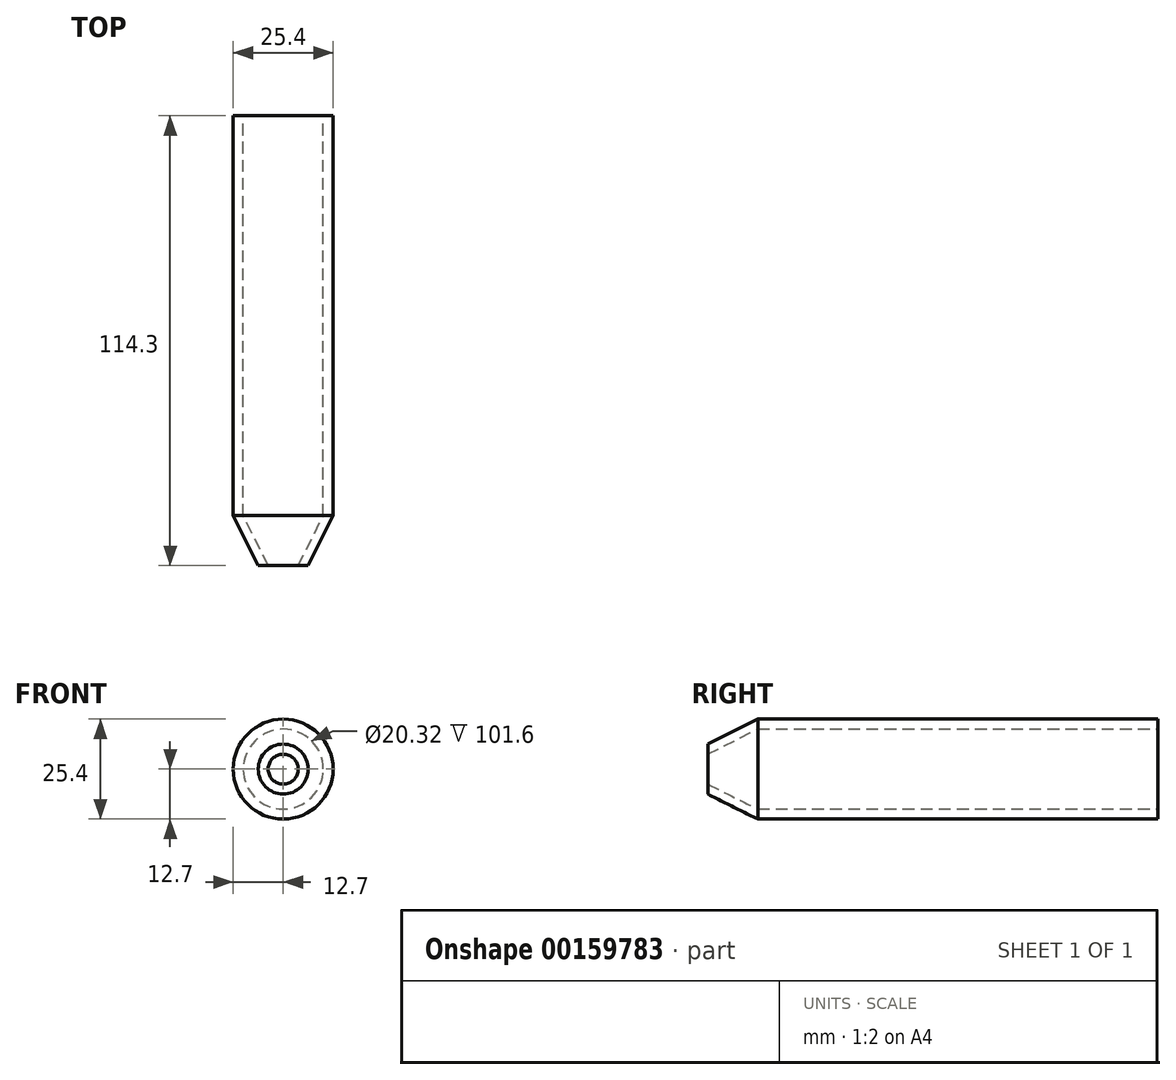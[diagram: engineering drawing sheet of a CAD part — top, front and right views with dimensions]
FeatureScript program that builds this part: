
annotation { "Feature Type Name" : "Feature", "Feature Type Description" : "" }
export const myFeature = defineFeature(function(context is Context, id is Id, definition is map)
    precondition{}
    {
        {
            var Q0;
            Q0=qCreatedBy(makeId("Front.planeOp"),FACE);
            var sketch = newSketch(context, id + "F0", { "sketchPlane" : qUnion([Q0])});
            skCircle(sketch, "E0", {"center": v(0, 0) * mm, "radius": 12.7 * mm});
            skCircle(sketch, "E1", {"center": v(0, 0) * mm, "radius": 10.16 * mm});
            skSolve(sketch);
        }
        {
            var Q0;
            Q0 = qSketchRegion(id + "F0", true);
            extrude(context, id + "F1", {"entities" : qUnion([Q0]), "depth" : 101.6 * mm, "offsetDistance" : 25.4 * mm});
        }
        {
            var Q0;
            Q0=makeQuery(id+"F1.opExtrude","CAP_FACE",FACE,{"disambiguationData":[OSD([sQuery(id+"F0.wireOp",EDGE,"E0"),sQuery(id+"F0.wireOp",EDGE,"E1")])],"isStart":false});
            cPlane(context, id + "F2", {"entities" : qUnion([Q0]), "cplaneType" : CPlaneType.OFFSET, "offset" : 6.35 * mm, "width" : 152.4 * mm, "height" : 152.4 * mm});
        }
        {
            var Q0;
            Q0=qCreatedBy(id+"F2.planeOp",FACE);
            cPlane(context, id + "F3", {"entities" : qUnion([Q0]), "cplaneType" : CPlaneType.OFFSET, "offset" : 6.35 * mm, "width" : 152.4 * mm, "height" : 152.4 * mm});
        }
        {
            var Q0;
            Q0=qCreatedBy(id+"F2.planeOp",FACE);
            var sketch = newSketch(context, id + "F4", { "sketchPlane" : qUnion([Q0])});
            skCircle(sketch, "E2", {"center": v(0, 0) * mm, "radius": 6.99 * mm});
            skCircle(sketch, "E3", {"center": v(0, 0) * mm, "radius": 9.53 * mm});
            skSolve(sketch);
        }
        {
            var Q0;
            Q0=qCreatedBy(id+"F3.planeOp",FACE);
            var sketch = newSketch(context, id + "F5", { "sketchPlane" : qUnion([Q0])});
            skCircle(sketch, "E4", {"center": v(0, 0) * mm, "radius": 6.35 * mm});
            skCircle(sketch, "E5", {"center": v(0, 0) * mm, "radius": 3.81 * mm});
            skSolve(sketch);
        }
        {
            var Q0;
            Q0=qCreatedBy(makeId("Right.planeOp"),FACE);
            var sketch = newSketch(context, id + "F6", { "sketchPlane" : qUnion([Q0])});
            skPoint(sketch, "E6.0", {"position": v(-114.3, 0) * mm});
            skPoint(sketch, "E7.0", {"position": v(-107.95, 0) * mm});
            skLineSegment(sketch, "E8", {"start": v(-114.3, 0) * mm, "end": v(-107.95, 0) * mm});
            skPoint(sketch, "E9.orphan", {"position": v(-101.6, 10.16) * mm});
            skPoint(sketch, "E10.0.start.orphan", {"position": v(-101.6, -10.16) * mm});
            skLineSegment(sketch, "E11.0", {"start": v(-114.3, -6.35) * mm, "end": v(-114.3, -3.81) * mm});
            skLineSegment(sketch, "E12.0", {"start": v(-101.6, -12.7) * mm, "end": v(-101.6, -10.16) * mm});
            skLineSegment(sketch, "E13", {"start": v(-101.6, -12.7) * mm, "end": v(-114.3, -6.35) * mm});
            skLineSegment(sketch, "E14", {"start": v(-114.3, -3.81) * mm, "end": v(-101.6, -10.16) * mm});
            skPoint(sketch, "E15.orphan", {"position": v(-107.95, 6.99) * mm});
            skPoint(sketch, "E16.0.start.orphan", {"position": v(-107.95, -6.99) * mm});
            skPoint(sketch, "E17.orphan", {"position": v(-101.6, 0) * mm});
            skPoint(sketch, "E18.trimOffspring.end.orphan", {"position": v(-107.95, 9.53) * mm});
            skPoint(sketch, "E19.trimOffspring.end.orphan", {"position": v(-101.6, 12.7) * mm});
            skPoint(sketch, "E20.0.start.orphan", {"position": v(-107.95, -9.53) * mm});
            skPoint(sketch, "E21.trimOffspring.end.orphan", {"position": v(-114.3, 6.35) * mm});
            skPoint(sketch, "E21.trimOffspring.start.orphan", {"position": v(-114.3, 3.8) * mm});
            skSolve(sketch);
        }
        {
            var Q0;
            Q0 = qSketchRegion(id + "F6", true);
            var Q1;
            Q1=sQuery(id+"F6.wireOp",EDGE,"E8");
            revolve(context, id + "F7", {"operationType" : NewBodyOperationType.ADD, "entities" : qUnion([Q0]), "axis" : qUnion([Q1]), "revolveType" : RevolveType.FULL});
        }
    });
